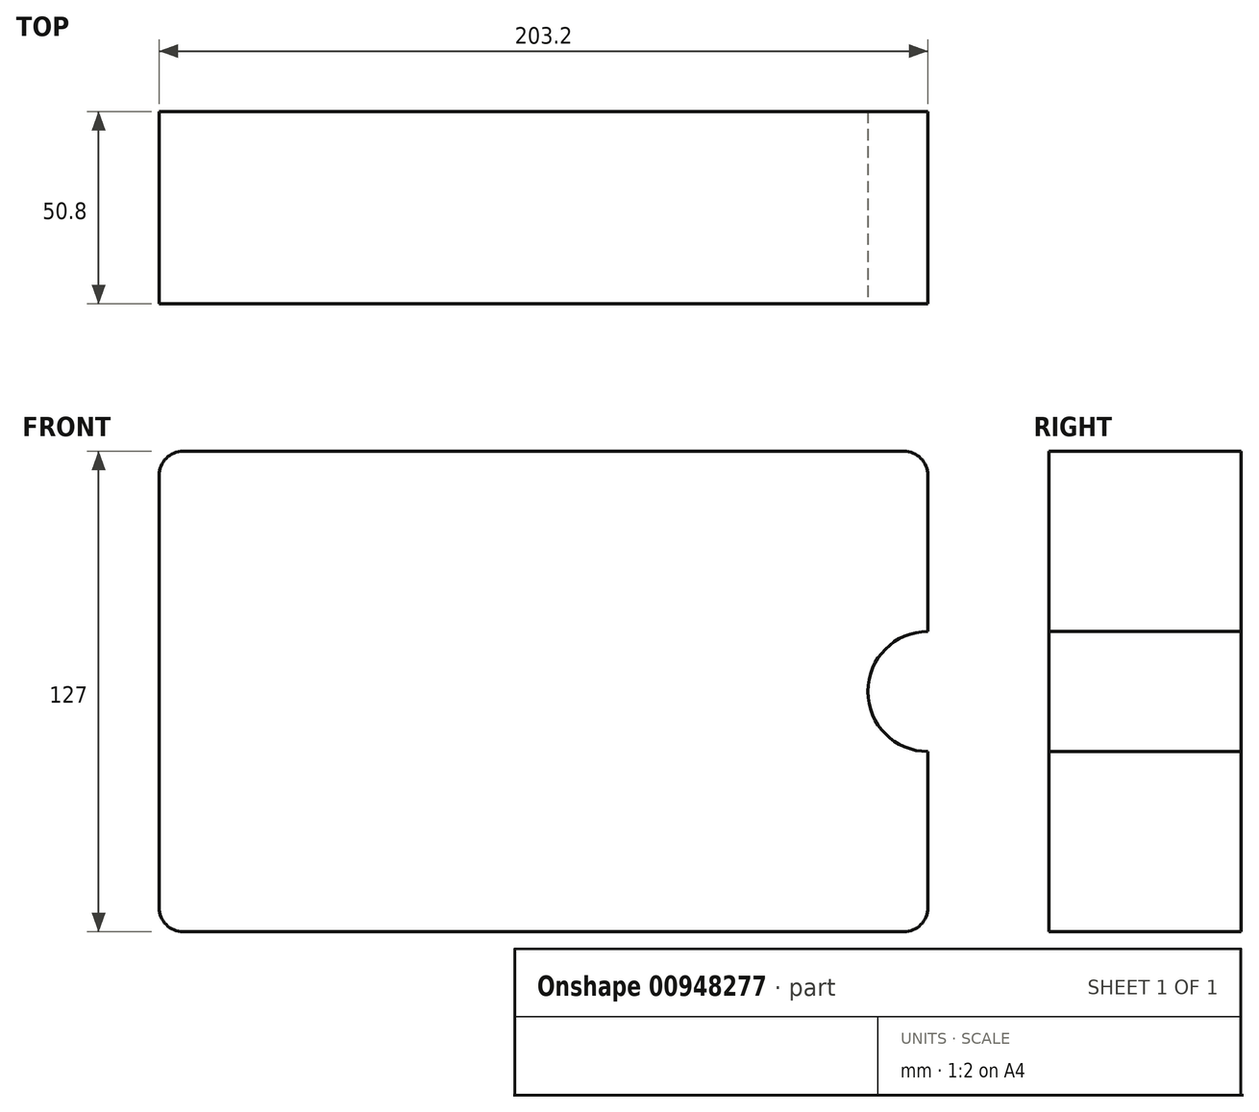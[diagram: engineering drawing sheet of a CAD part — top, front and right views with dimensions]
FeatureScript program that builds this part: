
annotation { "Feature Type Name" : "Feature", "Feature Type Description" : "" }
export const myFeature = defineFeature(function(context is Context, id is Id, definition is map)
    precondition{}
    {
        {
            var Q0;
            Q0=qCreatedBy(makeId("Front.planeOp"),FACE);
            var sketch = newSketch(context, id + "F0", { "sketchPlane" : qUnion([Q0])});
            skLineSegment(sketch, "E0.bottom", {"start": v(0, 0) * mm, "end": v(203.2, 0) * mm});
            skLineSegment(sketch, "E0.top", {"start": v(0, 127) * mm, "end": v(203.2, 127) * mm});
            skLineSegment(sketch, "E0.left", {"start": v(0, 0) * mm, "end": v(0, 127) * mm});
            skLineSegment(sketch, "E0.right", {"start": v(203.2, 0) * mm, "end": v(203.2, 127) * mm});
            skSolve(sketch);
        }
        {
            var Q0;
            Q0 = qSketchRegion(id + "F0", true);
            extrude(context, id + "F1", {"entities" : qUnion([Q0]), "depth" : 50.8 * mm, "offsetDistance" : 25.4 * mm});
        }
        {
            var Q0;
            Q0=makeQuery(id+"F1.opExtrude","CAP_FACE",FACE,{"disambiguationData":[OSD([sQuery(id+"F0.wireOp",EDGE,"E0.bottom"),sQuery(id+"F0.wireOp",EDGE,"E0.top"),sQuery(id+"F0.wireOp",EDGE,"E0.left"),sQuery(id+"F0.wireOp",EDGE,"E0.right")])],"isStart":false});
            var sketch = newSketch(context, id + "F2", { "sketchPlane" : qUnion([Q0])});
            skCircle(sketch, "E1", {"center": v(203.2, 63.5) * mm, "radius": 15.88 * mm});
            skSolve(sketch);
        }
        {
            var Q0;
            Q0 = qSketchRegion(id + "F2", true);
            extrude(context, id + "F3", {"entities" : qUnion([Q0]), "operationType" : NewBodyOperationType.REMOVE, "endBound" : BoundingType.THROUGH_ALL, "oppositeDirection" : true, "depth" : 25.4 * mm, "offsetDistance" : 25.4 * mm});
        }
        {
            var Q0;
            Q0=makeQuery(id+"F1.opExtrude","SWEPT_EDGE",EDGE,{"disambiguationData":[OSD([sQuery(id+"F0.wireOp",EDGE,"E0.top"),sQuery(id+"F0.wireOp",EDGE,"E0.right")])]});
            var Q1;
            Q1=makeQuery(id+"F1.opExtrude","SWEPT_EDGE",EDGE,{"disambiguationData":[OSD([sQuery(id+"F0.wireOp",EDGE,"E0.bottom"),sQuery(id+"F0.wireOp",EDGE,"E0.right")])]});
            var Q2;
            Q2=makeQuery(id+"F1.opExtrude","SWEPT_EDGE",EDGE,{"disambiguationData":[OSD([sQuery(id+"F0.wireOp",EDGE,"E0.top"),sQuery(id+"F0.wireOp",EDGE,"E0.left")])]});
            var Q3;
            Q3=makeQuery(id+"F1.opExtrude","SWEPT_EDGE",EDGE,{"disambiguationData":[OSD([sQuery(id+"F0.wireOp",EDGE,"E0.bottom"),sQuery(id+"F0.wireOp",EDGE,"E0.left")])]});
            fillet(context, id + "F4", {"entities" : qUnion([Q0, Q1, Q2, Q3]), "radius" : 6.35 * mm, "tangentPropagation" : true, "allowEdgeOverflow" : false});
        }
    });
